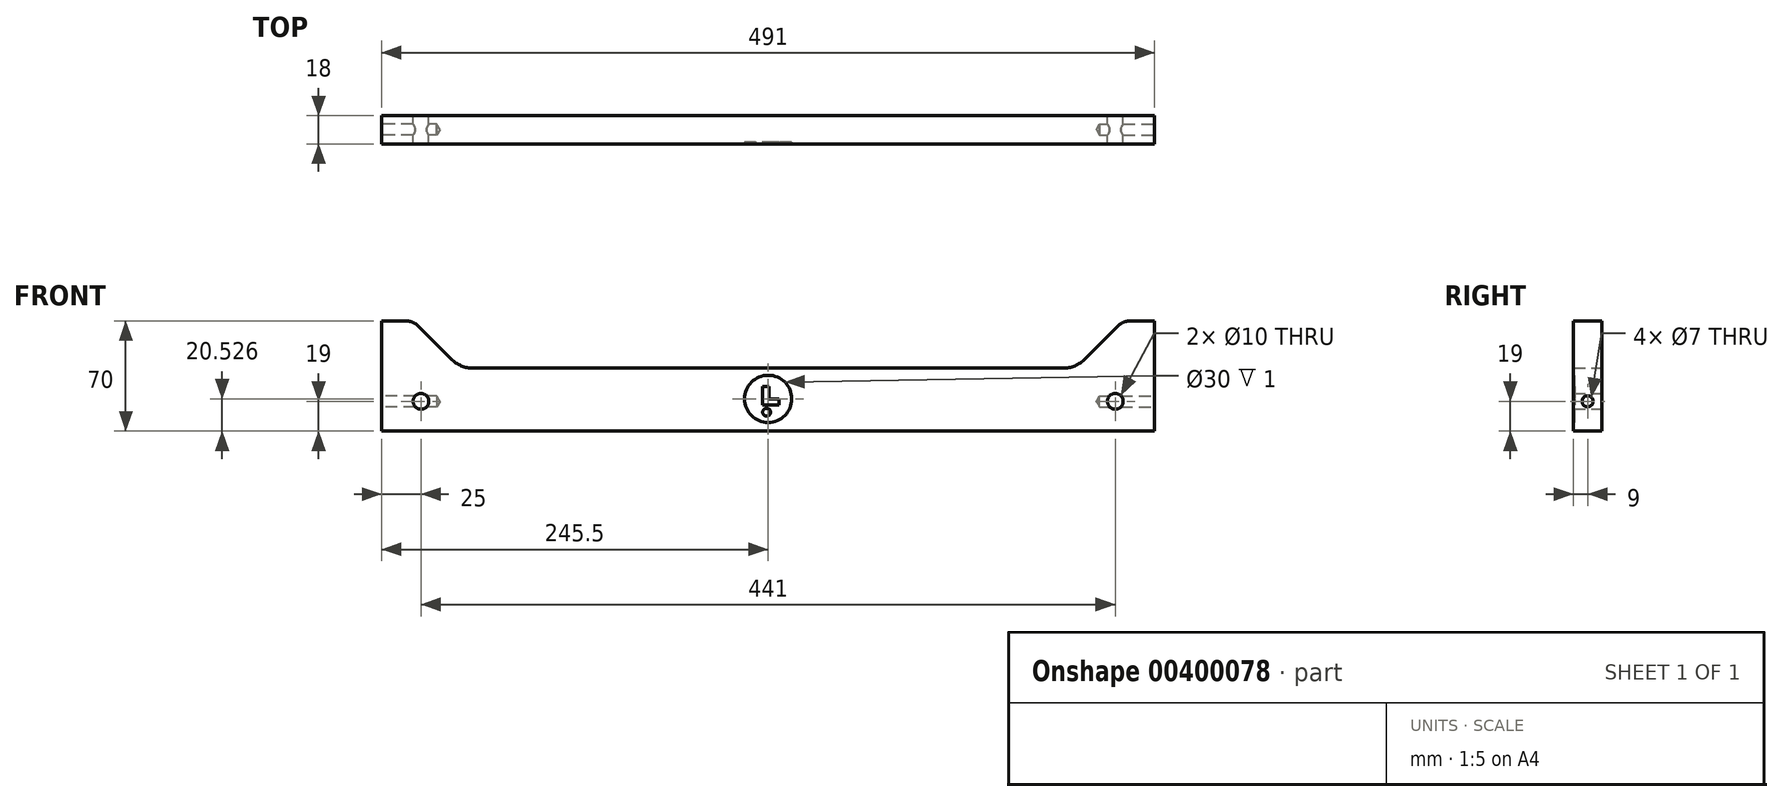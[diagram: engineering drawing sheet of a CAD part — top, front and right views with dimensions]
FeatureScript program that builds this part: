
annotation { "Feature Type Name" : "Feature", "Feature Type Description" : "" }
export const myFeature = defineFeature(function(context is Context, id is Id, definition is map)
    precondition{}
    {
        {
            var Q0;
            Q0=qCreatedBy(makeId("Front.planeOp"),FACE);
            var sketch = newSketch(context, id + "F0", { "sketchPlane" : qUnion([Q0])});
            skLineSegment(sketch, "E0", {"start": v(0, 0) * mm, "end": v(491, 0) * mm});
            skLineSegment(sketch, "E1", {"start": v(491, 0) * mm, "end": v(491, 70) * mm});
            skLineSegment(sketch, "E2", {"start": v(491, 70) * mm, "end": v(475.14, 70) * mm});
            skLineSegment(sketch, "E3", {"start": v(0, 70) * mm, "end": v(0, 0) * mm});
            skLineSegment(sketch, "E4", {"start": v(58.28, 40) * mm, "end": v(432.72, 40) * mm});
            skLineSegment(sketch, "E5", {"start": v(446.86, 45.86) * mm, "end": v(468.07, 67.07) * mm});
            skLineSegment(sketch, "E6", {"start": v(44.14, 45.86) * mm, "end": v(22.93, 67.07) * mm});
            skLineSegment(sketch, "E7.trimOffspring", {"start": v(15.86, 70) * mm, "end": v(0, 70) * mm});
            skPoint(sketch, "E8.visualSharp", {"position": v(50, 40) * mm});
            skArc(sketch, "E8.filletArc", {"start": v(44.14, 45.86) * mm, "mid": v(50.63, 41.52) * mm, "end": v(58.28, 40) * mm});
            skPoint(sketch, "E9.visualSharp", {"position": v(20, 70) * mm});
            skArc(sketch, "E9.filletArc", {"start": v(22.93, 67.07) * mm, "mid": v(19.68, 69.24) * mm, "end": v(15.86, 70) * mm});
            skPoint(sketch, "E10.visualSharp", {"position": v(441, 40) * mm});
            skArc(sketch, "E10.filletArc", {"start": v(432.72, 40) * mm, "mid": v(440.37, 41.52) * mm, "end": v(446.86, 45.86) * mm});
            skPoint(sketch, "E11.visualSharp", {"position": v(471, 70) * mm});
            skArc(sketch, "E11.filletArc", {"start": v(475.14, 70) * mm, "mid": v(471.32, 69.24) * mm, "end": v(468.07, 67.07) * mm});
            skCircle(sketch, "E12", {"center": v(25, 19) * mm, "radius": 5 * mm});
            skCircle(sketch, "E13", {"center": v(466, 19) * mm, "radius": 5 * mm});
            skSolve(sketch);
        }
        {
            var Q0;
            Q0 = qSketchRegion(id + "F0", true);
            extrude(context, id + "F1", {"entities" : qUnion([Q0]), "depth" : 18 * mm});
        }
        {
            var Q0;
            Q0=makeQuery(id+"F1.opExtrude","SWEPT_FACE",FACE,{"disambiguationData":[OSD([sQuery(id+"F0.wireOp",EDGE,"E1")])]});
            var sketch = newSketch(context, id + "F2", { "sketchPlane" : qUnion([Q0])});
            skCircle(sketch, "E14", {"center": v(-9, 19) * mm, "radius": 3.5 * mm});
            skSolve(sketch);
        }
        {
            var Q0;
            Q0=makeQuery(id+"F1.opExtrude","SWEPT_FACE",FACE,{"disambiguationData":[OSD([sQuery(id+"F0.wireOp",EDGE,"E3")])]});
            var sketch = newSketch(context, id + "F3", { "sketchPlane" : qUnion([Q0])});
            skCircle(sketch, "E15", {"center": v(9, 19) * mm, "radius": 3.5 * mm});
            skSolve(sketch);
        }
        {
            var Q0;
            Q0=sQuery(id+"F3.wireOp",VERTEX,"E15.center");
            var Q1;
            Q1=makeQuery(id+"F1.opExtrude","SWEPT_BODY",BODY,{"disambiguationData":[OSD([sQuery(id+"F0.wireOp",EDGE,"E0"),sQuery(id+"F0.wireOp",EDGE,"E1"),sQuery(id+"F0.wireOp",EDGE,"E2"),sQuery(id+"F0.wireOp",EDGE,"E3"),sQuery(id+"F0.wireOp",EDGE,"E4"),sQuery(id+"F0.wireOp",EDGE,"E5"),sQuery(id+"F0.wireOp",EDGE,"E6"),sQuery(id+"F0.wireOp",EDGE,"E7.trimOffspring"),sQuery(id+"F0.wireOp",EDGE,"E8.filletArc"),sQuery(id+"F0.wireOp",EDGE,"E9.filletArc"),sQuery(id+"F0.wireOp",EDGE,"E10.filletArc"),sQuery(id+"F0.wireOp",EDGE,"E11.filletArc"),sQuery(id+"F0.wireOp",EDGE,"E12"),sQuery(id+"F0.wireOp",EDGE,"E13")])]});
            hole(context, id + "F4", {"style" : HoleStyle.SIMPLE, "endStyle" : HoleEndStyle.BLIND, "holeDiameter" : 7 * mm, "holeDepth" : 35 * mm, "isTappedThrough" : true, "tappedDepth" : 12 * mm, "tapClearance" : 3, "locations" : qUnion([Q0]), "scope" : qUnion([Q1])});
        }
        {
            var Q0;
            Q0=sQuery(id+"F2.wireOp",VERTEX,"E14.center");
            var Q1;
            Q1=makeQuery(id+"F1.opExtrude","SWEPT_BODY",BODY,{"disambiguationData":[OSD([sQuery(id+"F0.wireOp",EDGE,"E0"),sQuery(id+"F0.wireOp",EDGE,"E1"),sQuery(id+"F0.wireOp",EDGE,"E2"),sQuery(id+"F0.wireOp",EDGE,"E3"),sQuery(id+"F0.wireOp",EDGE,"E4"),sQuery(id+"F0.wireOp",EDGE,"E5"),sQuery(id+"F0.wireOp",EDGE,"E6"),sQuery(id+"F0.wireOp",EDGE,"E7.trimOffspring"),sQuery(id+"F0.wireOp",EDGE,"E8.filletArc"),sQuery(id+"F0.wireOp",EDGE,"E9.filletArc"),sQuery(id+"F0.wireOp",EDGE,"E10.filletArc"),sQuery(id+"F0.wireOp",EDGE,"E11.filletArc"),sQuery(id+"F0.wireOp",EDGE,"E12"),sQuery(id+"F0.wireOp",EDGE,"E13")])]});
            hole(context, id + "F5", {"style" : HoleStyle.SIMPLE, "endStyle" : HoleEndStyle.BLIND, "holeDiameter" : 7 * mm, "holeDepth" : 35 * mm, "isTappedThrough" : true, "tappedDepth" : 12 * mm, "tapClearance" : 3, "locations" : qUnion([Q0]), "scope" : qUnion([Q1])});
        }
        {
            var Q0;
            Q0=makeQuery(id+"F1.opExtrude","CAP_FACE",FACE,{"disambiguationData":[OSD([sQuery(id+"F0.wireOp",EDGE,"E0"),sQuery(id+"F0.wireOp",EDGE,"E1"),sQuery(id+"F0.wireOp",EDGE,"E2"),sQuery(id+"F0.wireOp",EDGE,"E3"),sQuery(id+"F0.wireOp",EDGE,"E4"),sQuery(id+"F0.wireOp",EDGE,"E5"),sQuery(id+"F0.wireOp",EDGE,"E6"),sQuery(id+"F0.wireOp",EDGE,"E7.trimOffspring"),sQuery(id+"F0.wireOp",EDGE,"E8.filletArc"),sQuery(id+"F0.wireOp",EDGE,"E9.filletArc"),sQuery(id+"F0.wireOp",EDGE,"E10.filletArc"),sQuery(id+"F0.wireOp",EDGE,"E11.filletArc"),sQuery(id+"F0.wireOp",EDGE,"E12"),sQuery(id+"F0.wireOp",EDGE,"E13")])],"isStart":false});
            var sketch = newSketch(context, id + "F6", { "sketchPlane" : qUnion([Q0])});
            skCircle(sketch, "E16", {"center": v(245.5, 20.53) * mm, "radius": 15 * mm});
            skLineSegment(sketch, "E17", {"start": v(242.05, 28.53) * mm, "end": v(246.05, 28.53) * mm});
            skLineSegment(sketch, "E18", {"start": v(246.05, 28.53) * mm, "end": v(246.05, 20.53) * mm});
            skLineSegment(sketch, "E19", {"start": v(246.05, 20.53) * mm, "end": v(252.54, 20.53) * mm});
            skLineSegment(sketch, "E20", {"start": v(252.54, 20.53) * mm, "end": v(252.54, 16.53) * mm});
            skLineSegment(sketch, "E21", {"start": v(252.54, 16.53) * mm, "end": v(242.05, 16.53) * mm});
            skLineSegment(sketch, "E22", {"start": v(242.05, 28.53) * mm, "end": v(242.05, 16.53) * mm});
            skCircle(sketch, "E23", {"center": v(244.55, 12.04) * mm, "radius": 2.5 * mm});
            skSolve(sketch);
        }
        {
            var Q0;
            Q0 = qSketchRegion(id + "F6", true);
            extrude(context, id + "F7", {"entities" : qUnion([Q0]), "operationType" : NewBodyOperationType.REMOVE, "oppositeDirection" : true, "depth" : 1 * mm});
        }
    });
